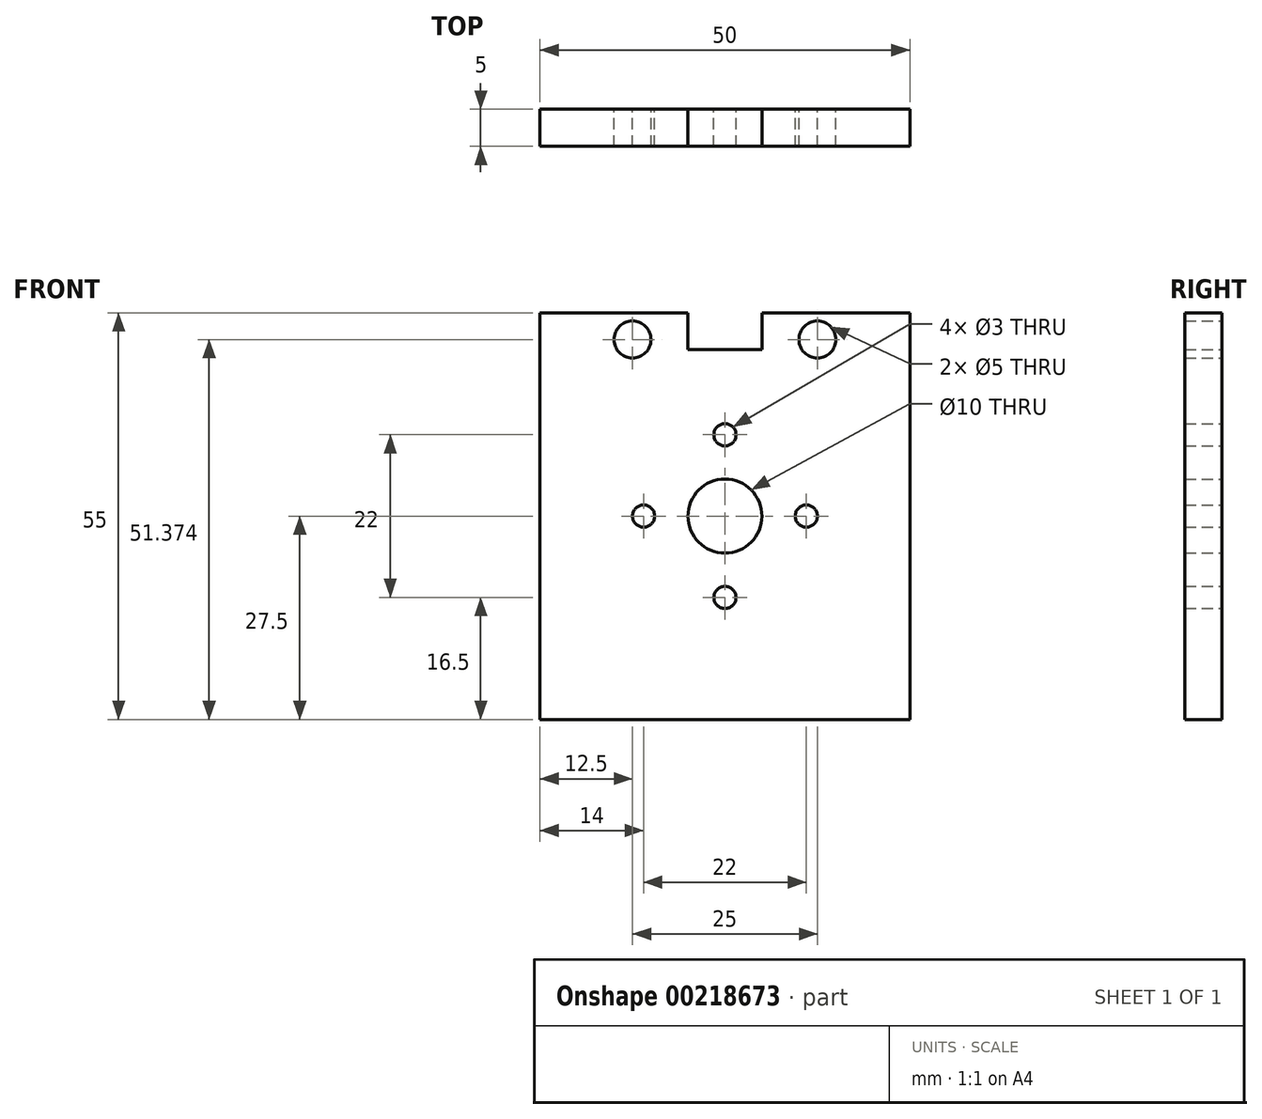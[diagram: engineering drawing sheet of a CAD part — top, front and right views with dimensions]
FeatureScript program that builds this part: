
annotation { "Feature Type Name" : "Feature", "Feature Type Description" : "" }
export const myFeature = defineFeature(function(context is Context, id is Id, definition is map)
    precondition{}
    {
        {
            var Q0;
            Q0=qCreatedBy(makeId("Front.planeOp"),FACE);
            var sketch = newSketch(context, id + "F0", { "sketchPlane" : qUnion([Q0])});
            skLineSegment(sketch, "E0.bottom", {"start": v(25, 27.5) * mm, "end": v(-25, 27.5) * mm});
            skLineSegment(sketch, "E0.top", {"start": v(25, -27.5) * mm, "end": v(-25, -27.5) * mm});
            skLineSegment(sketch, "E0.left", {"start": v(25, 27.5) * mm, "end": v(25, -27.5) * mm});
            skLineSegment(sketch, "E0.right", {"start": v(-25, 27.5) * mm, "end": v(-25, -27.5) * mm});
            skPoint(sketch, "E0.middle", {"position": v(0, 0) * mm});
            skCircle(sketch, "E1", {"center": v(0, 0) * mm, "radius": 5 * mm});
            skCircle(sketch, "E2", {"center": v(-12.5, 23.87) * mm, "radius": 2.5 * mm});
            skCircle(sketch, "E3.MirrorC", {"center": v(12.5, 23.87) * mm, "radius": 2.5 * mm});
            skLineSegment(sketch, "E4", {"start": v(-7.78, -27.5) * mm, "end": v(-17.78, -27.5) * mm});
            skCircle(sketch, "E5", {"center": v(11, 0) * mm, "radius": 1.5 * mm});
            skCircle(sketch, "E6.MirrorC", {"center": v(-11, 0) * mm, "radius": 1.5 * mm});
            skCircle(sketch, "E7", {"center": v(0, 11) * mm, "radius": 1.5 * mm});
            skLineSegment(sketch, "E8", {"start": v(0, 0) * mm, "end": v(0, 28.48) * mm, "construction": true});
            skPoint(sketch, "E8.endSnap0", {"position": v(0, 27.5) * mm});
            skCircle(sketch, "E9.MirrorC", {"center": v(0, -11) * mm, "radius": 1.5 * mm});
            skLineSegment(sketch, "E10", {"start": v(-5, 27.5) * mm, "end": v(-5, 22.5) * mm});
            skLineSegment(sketch, "E11.MirrorCS", {"start": v(5, 27.5) * mm, "end": v(5, 22.5) * mm});
            skLineSegment(sketch, "E12", {"start": v(-5, 22.5) * mm, "end": v(5, 22.5) * mm});
            skSolve(sketch);
        }
        {
            var Q0;
            Q0=makeQuery(id+"F0.imprint","IMPRINT",FACE,{"disambiguationData":[TD([[makeQuery(id+"F0.imprint","IMPRINT",EDGE,{"derivedFrom":sQuery(id+"F0.wireOp",EDGE,"E0.bottom")}),1.0]])]});
            extrude(context, id + "F1", {"entities" : qUnion([Q0]), "depth" : 5 * mm});
        }
    });
